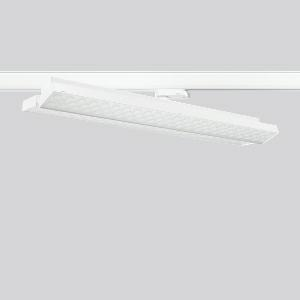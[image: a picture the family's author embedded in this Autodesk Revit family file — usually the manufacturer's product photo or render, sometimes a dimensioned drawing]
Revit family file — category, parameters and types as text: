
# Revit family: tx-move_742163_002_2_0791
name_source: partatom
category: Lighting Fixtures
units: mm (PartAtom-declared; Revit-internal decimal feet)

## family parameters
Cut with Voids When Loaded = No
Host = Face
Light Source = No
Part Type = Normal
Room Calculation Point = No
Round Connector Dimension = Use Diameter
Shared = No

## types (1)
- MultiLumen 1 (1 x LED Modul 927, 2000 lm, 2700)
    Apparent Load = 38 VA
    CIE Flux Codes = 65 90 98 100 100
    Color Rendering = 92
    Color Temperature = 2700
    Default Elevation = 1800 mm
    Description = Series: TX-MOVE
Multifunctional surface-mounted spotlight for area lighting. Very flat design. Housing: sheet steel, powder-coated. Rotation range: 356°. Swivel range: 90°. Consistent alignment possible with visible tilt scale. High-efficiency LED units with optimum light control thanks to clear plastic (PC) lens optics. Spezielle Mikrostrukturen reduzieren Gelbsaum. Asymmetrical light distribution. Best colour rendering with CRI >90 for fresh products and coloured textiles. With multi adaptor for 3-circuit tracks 230 V. Suitable for Track on ceiling. MultiLumen: Luminous flux adjustable in 3 steps. Factory setting is the highest luminous flux. Environmentally friendly and resource-saving due to replaceable and recyclable components. 
Colour: traffic white, matt (RAL 9016)
Length: 570 mm
Width: 119 mm
Height: 92 mm
Lamp: LED
Socket: without socket
Colour temperature: 2700K
Colour rendering index (CRI): 90
System power: 38 W
Rated luminous flux: 4000 lm
Luminous efficiency: 105 lm/W
System power 2: 51 W
Rated luminous flux 2: 5250 lm
Luminous efficiency 2: 103 lm/W
System power 3: 62 W
Rated luminous flux 3: 6200 lm
Luminous efficiency 3: 100 lm/W
Control gear: Regulated power supply
Protection class: I
Type of protection: IP 20
    Height = 75 mm
    Lamp = 1 x LED Modul 927
    Lamp Light Flux = 2000 lm
    Lamp count = 1
    Length = 569 mm
    Lifetime = 50000 h
    Luminous efficacy = 105 lm/W
    Manufacturer = RZB
    ModVariant = No
    Model = 742163.002.2
    Mounting Place = Ceiling
    Mounting Type = Surface mounted
    Number of Poles = 1
    OnlyDefault = Yes
    Power Factor = 1
    Product Name = TX-MOVE
    Product group = Track mounted projectors
    ProductGroupID = 301
    Protection Class = Protection class I
    Protection Degree = IP 20
    RLX_Detail_Level = 1
    RLX_Emergency_Light_Flux = 0 lm
    RLX_Emergency_Type = 0
    RLX_Emergency_Type_DB = No
    RlxData = <blob elided: 51957 chars, md5=6db0cd63>
    Socket = socket
    Standby Power = 0 W
    System Light Flux = 4000 lm
    System Power = 38 W
    Type Comments = MultiLumen 1
    Type Image = 742162.002.jpg
    URL = http://relux.com
    VarID = multilumen_1
    Voltage = 0 V
    Weight = 0.00 kg
    Width = 119 mm

## geometry (parser evidence)
native form markers: Blend x4, Sweep x15
no freeform markers — native parametric forms only
